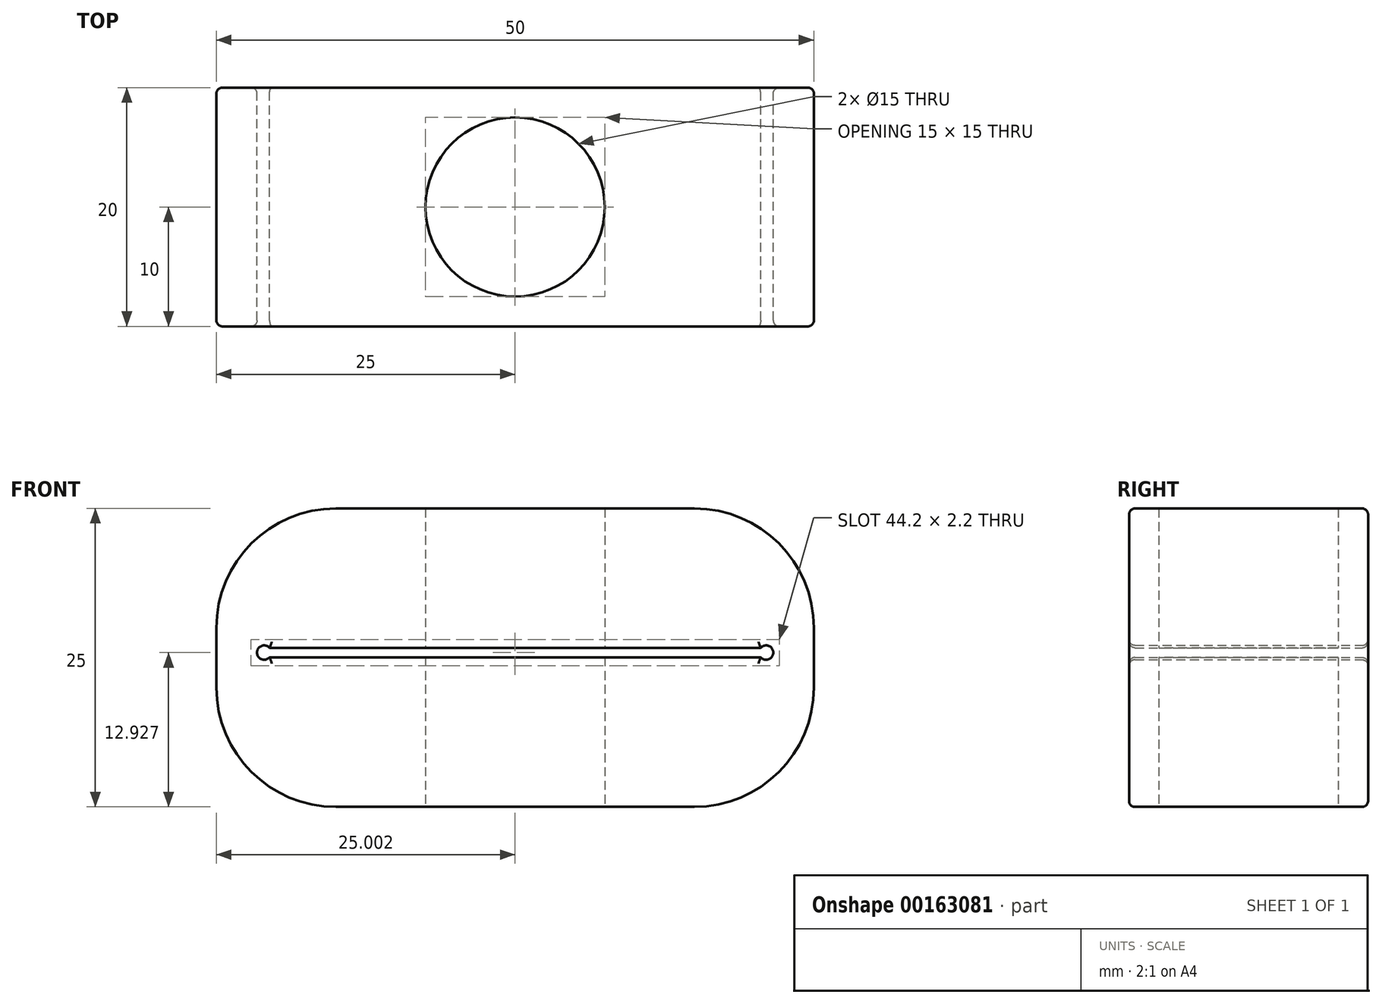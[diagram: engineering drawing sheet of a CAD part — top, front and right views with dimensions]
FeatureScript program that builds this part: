
annotation { "Feature Type Name" : "Feature", "Feature Type Description" : "" }
export const myFeature = defineFeature(function(context is Context, id is Id, definition is map)
    precondition{}
    {
        {
            var Q0;
            Q0=qCreatedBy(makeId("Top.planeOp"),FACE);
            var sketch = newSketch(context, id + "F0", { "sketchPlane" : qUnion([Q0])});
            skCircle(sketch, "E0", {"center": v(0, 0) * mm, "radius": 7.5 * mm});
            skLineSegment(sketch, "E1.bottom", {"start": v(25, -10) * mm, "end": v(-25, -10) * mm});
            skLineSegment(sketch, "E1.top", {"start": v(25, 10) * mm, "end": v(-25, 10) * mm});
            skLineSegment(sketch, "E1.left", {"start": v(25, -10) * mm, "end": v(25, 10) * mm});
            skLineSegment(sketch, "E1.right", {"start": v(-25, -10) * mm, "end": v(-25, 10) * mm});
            skSolve(sketch);
        }
        {
            var Q0;
            Q0 = qSketchRegion(id + "F0", true);
            extrude(context, id + "F1", {"entities" : qUnion([Q0]), "depth" : 25 * mm});
        }
        {
            var Q0;
            Q0=makeQuery(id+"F1.opExtrude","SWEPT_FACE",FACE,{"disambiguationData":[OSD([sQuery(id+"F0.wireOp",EDGE,"E1.top")])]});
            var sketch = newSketch(context, id + "F2", { "sketchPlane" : qUnion([Q0])});
            skLineSegment(sketch, "E2.bottom", {"start": v(-21, 13.33) * mm, "end": v(21, 13.33) * mm});
            skLineSegment(sketch, "E2.top", {"start": v(-21, 12.53) * mm, "end": v(21, 12.53) * mm});
            skLineSegment(sketch, "E2.left", {"start": v(-21, 13.33) * mm, "end": v(-21, 12.53) * mm});
            skLineSegment(sketch, "E2.right", {"start": v(21, 13.33) * mm, "end": v(21, 12.53) * mm});
            skPoint(sketch, "E2.middle", {"position": v(0, 12.93) * mm});
            skCircle(sketch, "E3", {"center": v(21, 12.93) * mm, "radius": 0.6 * mm});
            skCircle(sketch, "E4", {"center": v(-21, 12.93) * mm, "radius": 0.6 * mm});
            skSolve(sketch);
        }
        {
            var Q0;
            Q0 = qSketchRegion(id + "F2", true);
            extrude(context, id + "F3", {"entities" : qUnion([Q0]), "operationType" : NewBodyOperationType.REMOVE, "endBound" : BoundingType.THROUGH_ALL, "oppositeDirection" : true, "depth" : 25 * mm});
        }
        {
            var Q0;
            Q0=makeQuery(id+"F1.opExtrude","SWEPT_FACE",FACE,{"disambiguationData":[OSD([sQuery(id+"F0.wireOp",EDGE,"E1.top")])]});
            var Q1;
            Q1=makeQuery(id+"F1.opExtrude","SWEPT_FACE",FACE,{"disambiguationData":[OSD([sQuery(id+"F0.wireOp",EDGE,"E1.bottom")])]});
            fillet(context, id + "F4", {"entities" : qUnion([Q0, Q1]), "radius" : .5 * mm, "tangentPropagation" : true, "allowEdgeOverflow" : false});
        }
        {
            var Q0;
            Q0=makeQuery(id+"F1.opExtrude","CAP_EDGE",EDGE,{"disambiguationData":[OSD([sQuery(id+"F0.wireOp",EDGE,"E1.right")])],"isStart":false});
            var Q1;
            Q1=makeQuery(id+"F1.opExtrude","CAP_EDGE",EDGE,{"disambiguationData":[OSD([sQuery(id+"F0.wireOp",EDGE,"E1.left")])],"isStart":false});
            var Q2;
            Q2=makeQuery(id+"F1.opExtrude","CAP_EDGE",EDGE,{"disambiguationData":[OSD([sQuery(id+"F0.wireOp",EDGE,"E1.right")])],"isStart":true});
            var Q3;
            Q3=makeQuery(id+"F1.opExtrude","CAP_EDGE",EDGE,{"disambiguationData":[OSD([sQuery(id+"F0.wireOp",EDGE,"E1.left")])],"isStart":true});
            fillet(context, id + "F5", {"entities" : qUnion([Q0, Q1, Q2, Q3]), "radius" : 10 * mm, "tangentPropagation" : true, "allowEdgeOverflow" : false});
        }
    });
